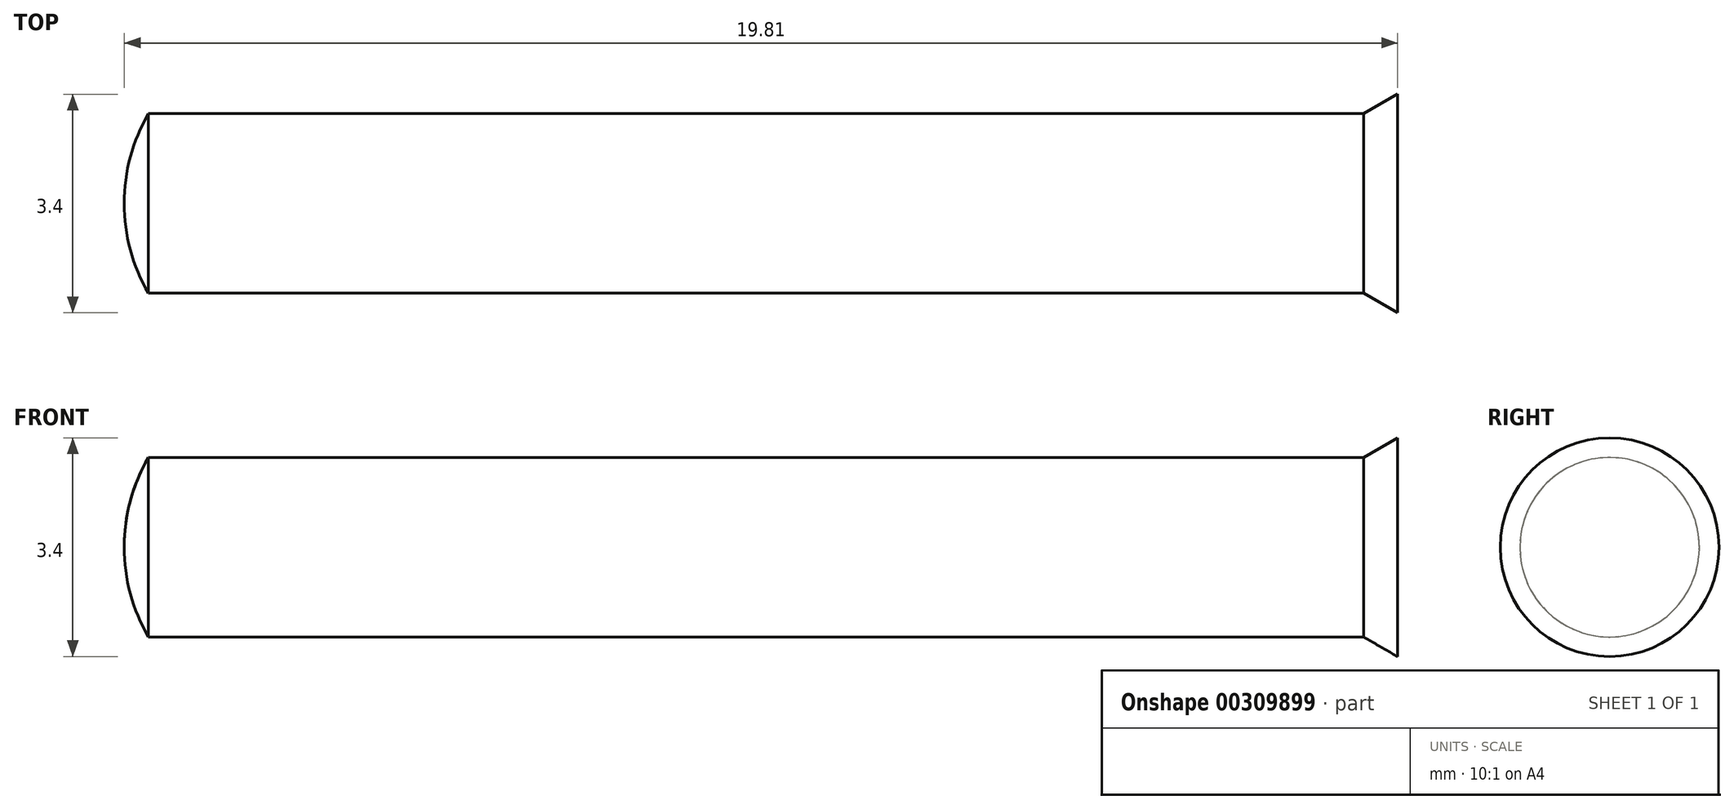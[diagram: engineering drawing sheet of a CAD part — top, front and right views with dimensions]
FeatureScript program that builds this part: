
annotation { "Feature Type Name" : "Feature", "Feature Type Description" : "" }
export const myFeature = defineFeature(function(context is Context, id is Id, definition is map)
    precondition{}
    {
        {
            var Q0;
            Q0=qCreatedBy(makeId("Front.planeOp"),FACE);
            var sketch = newSketch(context, id + "F0", { "sketchPlane" : qUnion([Q0])});
            skLineSegment(sketch, "E0", {"start": v(0, 0) * mm, "end": v(0, 1.7) * mm});
            skLineSegment(sketch, "E1", {"start": v(0, 1.7) * mm, "end": v(-0.53, 1.4) * mm});
            skLineSegment(sketch, "E2", {"start": v(-0.53, 1.4) * mm, "end": v(-19.44, 1.4) * mm});
            skLineSegment(sketch, "E3", {"start": v(-19.44, 1.4) * mm, "end": v(-19.44, 0) * mm, "construction": true});
            skArc(sketch, "E4", {"start": v(-19.44, 1.4) * mm, "mid": v(-19.72, 0.72) * mm, "end": v(-19.81, 0) * mm});
            skLineSegment(sketch, "E5", {"start": v(-19.81, 0) * mm, "end": v(0, 0) * mm, "construction": true});
            skSolve(sketch);
        }
        {
            var Q0;
            Q0=sQuery(id+"F0.wireOp",EDGE,"E4");
            var Q1;
            Q1=sQuery(id+"F0.wireOp",EDGE,"E2");
            var Q2;
            Q2=sQuery(id+"F0.wireOp",EDGE,"E1");
            var Q3;
            Q3=sQuery(id+"F0.wireOp",EDGE,"E0");
            var Q4;
            Q4=sQuery(id+"F0.wireOp",EDGE,"E5");
            revolve(context, id + "F1", {"bodyType" : ToolBodyType.SURFACE, "surfaceEntities" : qUnion([Q0, Q1, Q2, Q3]), "axis" : qUnion([Q4]), "revolveType" : RevolveType.FULL});
        }
    });
